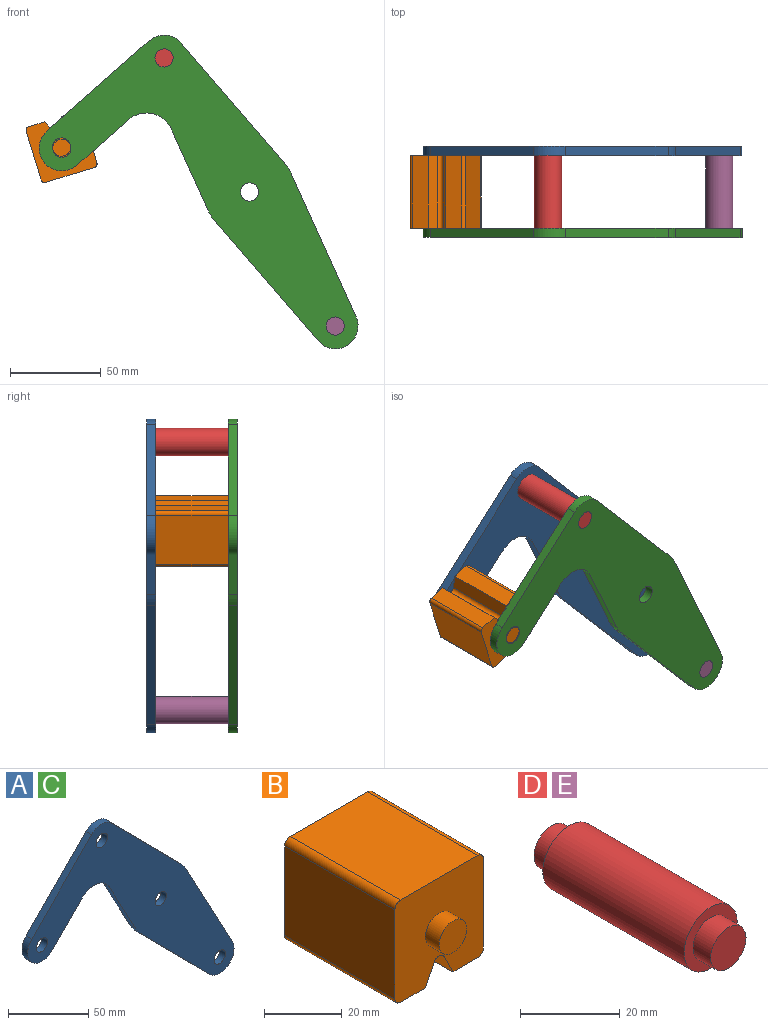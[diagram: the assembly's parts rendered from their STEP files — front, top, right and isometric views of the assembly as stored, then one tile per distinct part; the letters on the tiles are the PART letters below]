
ASSEMBLY  parts=5 mates=3
PART A: 18 faces, bbox 181.7x5x165.8 mm
  f0: plane 43.49x23.35mm, normal (-0.88,0,-0.47), area 246.8mm2, adj f1,f14,f16,f17
  f1: cylinder r=25mm len=5.75mm, axis (0,1,0), area 35.8mm2, adj f0,f2,f16,f17
  f2: plane 61.6x60.87mm, normal (-0.71,0,-0.7), area 433mm2, adj f1,f3,f16,f17
  f3: cylinder r=12.5mm len=21.39mm, axis (0,1,0), area 178.4mm2, adj f2,f4,f16,f17
  f4: plane 76.3x40.96mm, normal (0.88,0,0.47), area 433mm2, adj f3,f5,f16,f17
  f5: cylinder r=25mm len=5.75mm, axis (0,1,0), area 35.8mm2, adj f4,f6,f16,f17
  f6: plane 61.6x60.87mm, normal (0.71,0,0.7), area 433mm2, adj f5,f7,f16,f17
  f7: cylinder r=12.5mm len=17.78mm, axis (0,1,0), area 98.9mm2, adj f6,f8,f16,f17
  f8: plane 53.35x52.71mm, normal (-0.71,0,0.7), area 375mm2, adj f7,f9,f16,f17
  f9: cylinder r=12.5mm len=21.39mm, axis (0,1,0), area 196.3mm2, adj f8,f10,f16,f17
  f10: plane 26.86x26.54mm, normal (0.71,0,-0.7), area 188.8mm2, adj f9,f14,f16,f17
  f11: cylinder r=5mm len=10mm, axis (0,1,0), area 157.1mm2, adj f16,f17
  f12: cylinder r=5mm len=10mm, axis (0,1,0), area 157.1mm2, adj f16,f17
  f13: cylinder r=5mm len=10mm, axis (0,1,0), area 157.1mm2, adj f16,f17
  f14: cylinder r=15mm len=23.89mm, axis (0,1,0), area 140.2mm2, adj f0,f10,f16,f17
  f15: cylinder r=5mm len=10mm, axis (0,1,0), area 157.1mm2, adj f16,f17
  f16: plane 181.66x165.78mm, normal (0,-1,0), area 8710.1mm2, adj f0,f1,f2,f3,f4,f5,f6,f7
  f17: plane 181.66x165.78mm, normal (0,1,0), area 8710.1mm2, adj f0,f1,f2,f3,f4,f5,f6,f7
PART B: 18 faces, bbox 32.1x50x32.1 mm
  f0: plane 40x28.08mm, normal (1,0,0), area 1123.1mm2, adj f4,f10,f13,f14
  f1: plane 40x9.04mm, normal (0,0,-1), area 361.6mm2, adj f2,f4,f10,f14
  f2: plane 40x6.42mm, normal (-0.89,0,-0.45), area 287.2mm2, adj f1,f4,f10,f15
  f3: plane 40x6.42mm, normal (0.89,0,-0.45), area 287.2mm2, adj f4,f5,f10,f15
  f4: plane 32.08x32.08mm, normal (0,-1,0), area 900.6mm2, adj f0,f1,f2,f3,f5,f6,f7,f9
  f5: plane 40x9.04mm, normal (0,0,-1), area 361.6mm2, adj f3,f4,f10,f16
  f6: plane 40x28.08mm, normal (0,0,1), area 1123.1mm2, adj f4,f10,f13,f17
  f7: plane 40x28.08mm, normal (-1,0,0), area 1123.1mm2, adj f4,f10,f16,f17
  f8: plane 10x10mm, normal (0,-1,0), area 78.5mm2, adj f9
  f9: cylinder r=5mm len=10mm, axis (0,1,0), area 157.1mm2, adj f4,f8
  f10: plane 32.08x32.08mm, normal (0,1,0), area 900.6mm2, adj f0,f1,f2,f3,f5,f6,f7,f12
  f11: plane 10x10mm, normal (0,1,0), area 78.5mm2, adj f12
  f12: cylinder r=5mm len=10mm, axis (0,-1,0), area 157.1mm2, adj f10,f11
  f13: cylinder r=2mm len=40mm, axis (0,1,0), area 125.7mm2, adj f0,f4,f6,f10
  f14: cylinder r=2mm len=40mm, axis (0,-1,0), area 125.7mm2, adj f0,f1,f4,f10
  f15: cylinder r=2mm len=40mm, axis (0,1,0), area 177.1mm2, adj f2,f3,f4,f10
  f16: cylinder r=2mm len=40mm, axis (0,1,0), area 125.7mm2, adj f4,f5,f7,f10
  f17: cylinder r=2mm len=40mm, axis (0,-1,0), area 125.7mm2, adj f4,f6,f7,f10
PART C: same geometry as A
PART D: 7 faces, bbox 15x50x15 mm
  f0: cylinder r=7.5mm len=40mm, axis (0,-1,0), area 1885mm2, adj f2,f5
  f1: cylinder r=5mm len=10mm, axis (0,1,0), area 157.1mm2, adj f2,f3
  f2: plane 15x15mm, normal (0,-1,0), area 98.2mm2, adj f0,f1
  f3: plane 10x10mm, normal (0,-1,0), area 78.5mm2, adj f1
  f4: cylinder r=5mm len=10mm, axis (0,-1,0), area 157.1mm2, adj f5,f6
  f5: plane 15x15mm, normal (0,1,0), area 98.2mm2, adj f0,f4
  f6: plane 10x10mm, normal (0,1,0), area 78.5mm2, adj f4
PART E: same geometry as D
PLACE A rot(axis=(0,1,0),3.9deg) t=(20.22,4.31,26.55)mm
PLACE B rot(axis=(0,1,0),162.9deg) t=(-188.36,-40.69,36.86)mm
PLACE C rot(axis=(0,1,0),3.9deg) t=(20.22,-40.69,26.55)mm fixed
PLACE D rot(axis=(0,1,0),3.9deg) t=(20.22,-40.69,26.55)mm
PLACE E rot(axis=(0,1,0),3.9deg) t=(114.41,-40.69,-120.93)mm
MATE revolute B.f4 <-> C.f9  axis (0,-1,0) through (-83.08,-40.69,50.63)mm
MATE fastened C.f3 <-> E.f0  axis (0,1,0) through (67.32,-40.69,-47.19)mm
MATE fastened A.f7 <-> D.f0  axis (0,-1,0) through (-26.88,-0.69,100.3)mm
